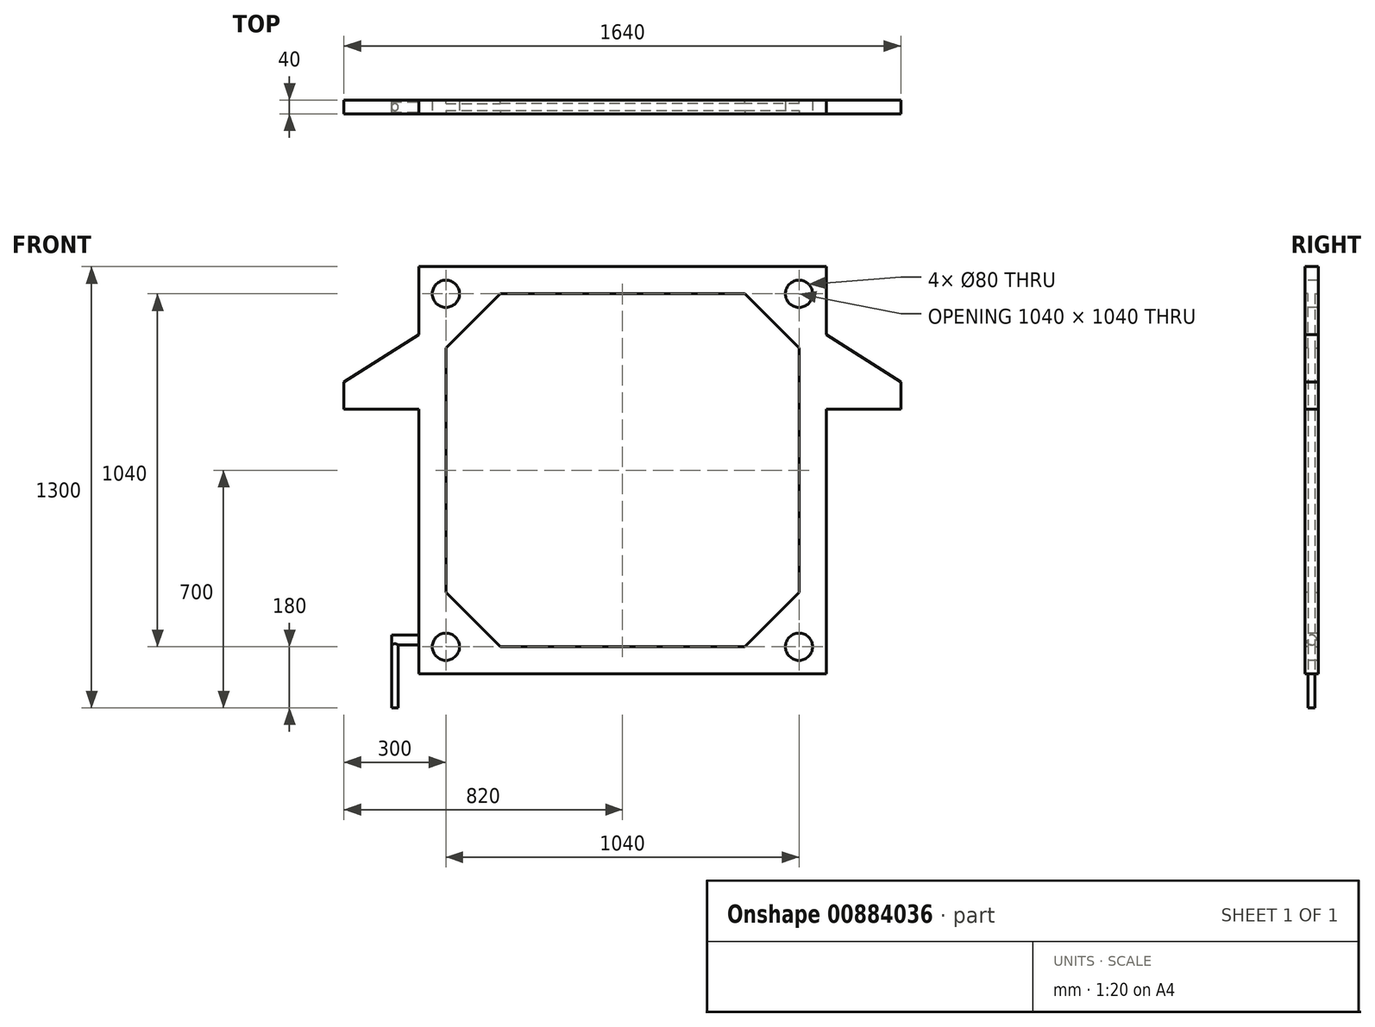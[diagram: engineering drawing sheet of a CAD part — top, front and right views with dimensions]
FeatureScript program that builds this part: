
annotation { "Feature Type Name" : "Feature", "Feature Type Description" : "" }
export const myFeature = defineFeature(function(context is Context, id is Id, definition is map)
    precondition{}
    {
        {
            var Q0;
            Q0=qCreatedBy(makeId("Front.planeOp"),FACE);
            var sketch = newSketch(context, id + "F0", { "sketchPlane" : qUnion([Q0])});
            skLineSegment(sketch, "E0.bottom", {"start": v(-600, 600) * mm, "end": v(600, 600) * mm});
            skLineSegment(sketch, "E0.top", {"start": v(-600, -600) * mm, "end": v(600, -600) * mm});
            skLineSegment(sketch, "E0.left", {"start": v(-600, 600) * mm, "end": v(-600, -600) * mm});
            skLineSegment(sketch, "E0.right", {"start": v(600, 600) * mm, "end": v(600, -600) * mm});
            skPoint(sketch, "E0.middle", {"position": v(0, 0) * mm});
            skLineSegment(sketch, "E1", {"start": v(600, 400) * mm, "end": v(820, 260) * mm});
            skLineSegment(sketch, "E2", {"start": v(820, 260) * mm, "end": v(820, 180) * mm});
            skLineSegment(sketch, "E3", {"start": v(820, 180) * mm, "end": v(600, 180) * mm});
            skLineSegment(sketch, "E4.MirrorCS", {"start": v(-820, 180) * mm, "end": v(-600, 180) * mm});
            skLineSegment(sketch, "E5.MirrorCS", {"start": v(-600, 400) * mm, "end": v(-820, 260) * mm});
            skLineSegment(sketch, "E6.MirrorCS", {"start": v(-820, 260) * mm, "end": v(-820, 180) * mm});
            skSolve(sketch);
        }
        {
            var Q0;
            Q0=qSketchRegion(id+"F0",true);
            extrude(context, id + "F1", {"entities" : qUnion([Q0]), "endBound" : BoundingType.SYMMETRIC, "depth" : 40 * mm, "offsetDistance" : 25 * mm});
        }
        {
            var Q0;
            Q0=makeQuery(id+"F1.opExtrude","CAP_FACE",FACE,{"disambiguationData":[OSD([sQuery(id+"F0.wireOp",EDGE,"E0.bottom"),sQuery(id+"F0.wireOp",EDGE,"E0.top"),sQuery(id+"F0.wireOp",EDGE,"E0.left"),sQuery(id+"F0.wireOp",EDGE,"E0.right"),sQuery(id+"F0.wireOp",EDGE,"E1"),sQuery(id+"F0.wireOp",EDGE,"E2"),sQuery(id+"F0.wireOp",EDGE,"E3"),sQuery(id+"F0.wireOp",EDGE,"E4.MirrorCS"),sQuery(id+"F0.wireOp",EDGE,"E5.MirrorCS"),sQuery(id+"F0.wireOp",EDGE,"E6.MirrorCS")])],"isStart":false});
            var sketch = newSketch(context, id + "F2", { "sketchPlane" : qUnion([Q0])});
            skCircle(sketch, "E7", {"center": v(-520, 520) * mm, "radius": 40 * mm});
            skCircle(sketch, "E8.0.1.0", {"center": v(-520, -520) * mm, "radius": 40 * mm});
            skCircle(sketch, "E8.1.0.0", {"center": v(520, 520) * mm, "radius": 40 * mm});
            skCircle(sketch, "E8.1.1.0", {"center": v(520, -520) * mm, "radius": 40 * mm});
            skLineSegment(sketch, "E8.direction1", {"start": v(-520, 520) * mm, "end": v(520, 520) * mm, "construction": true});
            skLineSegment(sketch, "E8.direction2", {"start": v(-520, 520) * mm, "end": v(-520, -520) * mm, "construction": true});
            skSolve(sketch);
        }
        {
            var Q0;
            Q0=qSketchRegion(id+"F2",true);
            extrude(context, id + "F3", {"entities" : qUnion([Q0]), "operationType" : NewBodyOperationType.REMOVE, "oppositeDirection" : true, "depth" : 50 * mm, "offsetDistance" : 25 * mm});
        }
        {
            var Q0;
            Q0=makeQuery(id+"F1.opExtrude","CAP_FACE",FACE,{"disambiguationData":[OSD([sQuery(id+"F0.wireOp",EDGE,"E0.bottom"),sQuery(id+"F0.wireOp",EDGE,"E0.top"),sQuery(id+"F0.wireOp",EDGE,"E0.left"),sQuery(id+"F0.wireOp",EDGE,"E0.right"),sQuery(id+"F0.wireOp",EDGE,"E1"),sQuery(id+"F0.wireOp",EDGE,"E2"),sQuery(id+"F0.wireOp",EDGE,"E3"),sQuery(id+"F0.wireOp",EDGE,"E4.MirrorCS"),sQuery(id+"F0.wireOp",EDGE,"E5.MirrorCS"),sQuery(id+"F0.wireOp",EDGE,"E6.MirrorCS")])],"isStart":false});
            var sketch = newSketch(context, id + "F4", { "sketchPlane" : qUnion([Q0])});
            skLineSegment(sketch, "E9.bottom", {"start": v(-360, 520) * mm, "end": v(360, 520) * mm});
            skLineSegment(sketch, "E9.top", {"start": v(-360, -520) * mm, "end": v(360, -520) * mm});
            skLineSegment(sketch, "E9.left", {"start": v(-520, 360) * mm, "end": v(-520, -360) * mm});
            skLineSegment(sketch, "E9.right", {"start": v(520, 360) * mm, "end": v(520, -360) * mm});
            skPoint(sketch, "E9.middle", {"position": v(0, 0) * mm});
            skLineSegment(sketch, "E10", {"start": v(-360, 520) * mm, "end": v(-520, 360) * mm});
            skLineSegment(sketch, "E11.1.0", {"start": v(-520, -360) * mm, "end": v(-360, -520) * mm});
            skLineSegment(sketch, "E11.2.0", {"start": v(360, -520) * mm, "end": v(520, -360) * mm});
            skLineSegment(sketch, "E11.3.0", {"start": v(520, 360) * mm, "end": v(360, 520) * mm});
            skPoint(sketch, "E12.orphan", {"position": v(-520, 520) * mm});
            skPoint(sketch, "E13.orphan", {"position": v(520, 520) * mm});
            skPoint(sketch, "E14.orphan", {"position": v(520, -520) * mm});
            skPoint(sketch, "E15.orphan", {"position": v(-520, -520) * mm});
            skSolve(sketch);
        }
        {
            var Q0;
            Q0=makeQuery(id+"F4.imprint","IMPRINT",FACE,{"disambiguationData":[TD([[makeQuery(id+"F4.imprint","IMPRINT",EDGE,{"derivedFrom":sQuery(id+"F4.wireOp",EDGE,"E9.bottom")}),-1.0]])]});
            extrude(context, id + "F5", {"entities" : qUnion([Q0]), "operationType" : NewBodyOperationType.REMOVE, "oppositeDirection" : true, "depth" : 10 * mm, "offsetDistance" : 25 * mm});
        }
        {
            var Q0;
            Q0=makeQuery(id+"F1.opExtrude","CAP_FACE",FACE,{"disambiguationData":[OSD([sQuery(id+"F0.wireOp",EDGE,"E0.bottom"),sQuery(id+"F0.wireOp",EDGE,"E0.top"),sQuery(id+"F0.wireOp",EDGE,"E0.left"),sQuery(id+"F0.wireOp",EDGE,"E0.right"),sQuery(id+"F0.wireOp",EDGE,"E1"),sQuery(id+"F0.wireOp",EDGE,"E2"),sQuery(id+"F0.wireOp",EDGE,"E3"),sQuery(id+"F0.wireOp",EDGE,"E4.MirrorCS"),sQuery(id+"F0.wireOp",EDGE,"E5.MirrorCS"),sQuery(id+"F0.wireOp",EDGE,"E6.MirrorCS")])],"isStart":true});
            var sketch = newSketch(context, id + "F6", { "sketchPlane" : qUnion([Q0])});
            skLineSegment(sketch, "E16.0.0", {"start": v(520, -360) * mm, "end": v(360, -520) * mm});
            skLineSegment(sketch, "E16.0.1", {"start": v(360, -520) * mm, "end": v(-360, -520) * mm});
            skLineSegment(sketch, "E16.0.2", {"start": v(-360, -520) * mm, "end": v(-520, -360) * mm});
            skLineSegment(sketch, "E16.0.3", {"start": v(-520, -360) * mm, "end": v(-520, 360) * mm});
            skLineSegment(sketch, "E16.0.4", {"start": v(-520, 360) * mm, "end": v(-360, 520) * mm});
            skLineSegment(sketch, "E16.0.5", {"start": v(-360, 520) * mm, "end": v(360, 520) * mm});
            skLineSegment(sketch, "E16.0.6", {"start": v(360, 520) * mm, "end": v(520, 360) * mm});
            skLineSegment(sketch, "E16.0.7", {"start": v(520, 360) * mm, "end": v(520, -360) * mm});
            skSolve(sketch);
        }
        {
            var Q0;
            Q0=makeQuery(id+"F6.imprint","IMPRINT",FACE,{"disambiguationData":[TD([[makeQuery(id+"F6.imprint","IMPRINT",EDGE,{"derivedFrom":sQuery(id+"F6.wireOp",EDGE,"E16.0.0")}),-1.0]])]});
            extrude(context, id + "F7", {"entities" : qUnion([Q0]), "operationType" : NewBodyOperationType.REMOVE, "oppositeDirection" : true, "depth" : 10 * mm, "offsetDistance" : 25 * mm});
        }
        {
            var Q0;
            {var subQ0=sQuery(id+"F0.wireOp",EDGE,"E0.left");Q0=makeQuery(id+"F1.opExtrude","SWEPT_FACE",FACE,{"disambiguationData":[OSD([subQ0]),TDD([makeQuery(id+"F0.imprint","IMPRINT",EDGE,{"disambiguationData":[TD([[makeQuery(id+"F0.imprint","INTERSECT",VERTEX,{"derivedFrom":[sQuery(id+"F0.wireOp",EDGE,"E0.top"),subQ0]}),1.0]])],"derivedFrom":subQ0})])]});}
            var sketch = newSketch(context, id + "F8", { "sketchPlane" : qUnion([Q0])});
            skCircle(sketch, "E17", {"center": v(0, -500) * mm, "radius": 15 * mm});
            skSolve(sketch);
        }
        {
            var Q0;
            Q0=makeQuery(id+"F8.imprint","IMPRINT",FACE,{"disambiguationData":[TD([[makeQuery(id+"F8.imprint","IMPRINT",EDGE,{"derivedFrom":sQuery(id+"F8.wireOp",EDGE,"E17")}),1.0]])]});
            extrude(context, id + "F9", {"entities" : qUnion([Q0]), "operationType" : NewBodyOperationType.ADD, "depth" : 80 * mm, "offsetDistance" : 25 * mm});
        }
        {
            var Q0;
            Q0=makeQuery(id+"F1.opExtrude","SWEPT_FACE",FACE,{"disambiguationData":[OSD([sQuery(id+"F0.wireOp",EDGE,"E0.top")])]});
            var sketch = newSketch(context, id + "F10", { "sketchPlane" : qUnion([Q0])});
            skCircle(sketch, "E18", {"center": v(-670, 0) * mm, "radius": 10 * mm});
            skSolve(sketch);
        }
        {
            var Q0;
            Q0=qSketchRegion(id+"F10",true);
            extrude(context, id + "F11", {"entities" : qUnion([Q0]), "operationType" : NewBodyOperationType.ADD, "oppositeDirection" : true, "depth" : 100 * mm, "offsetDistance" : 25 * mm, "hasSecondDirection" : true, "secondDirectionOppositeDirection" : false, "secondDirectionDepth" : 100 * mm});
        }
    });
